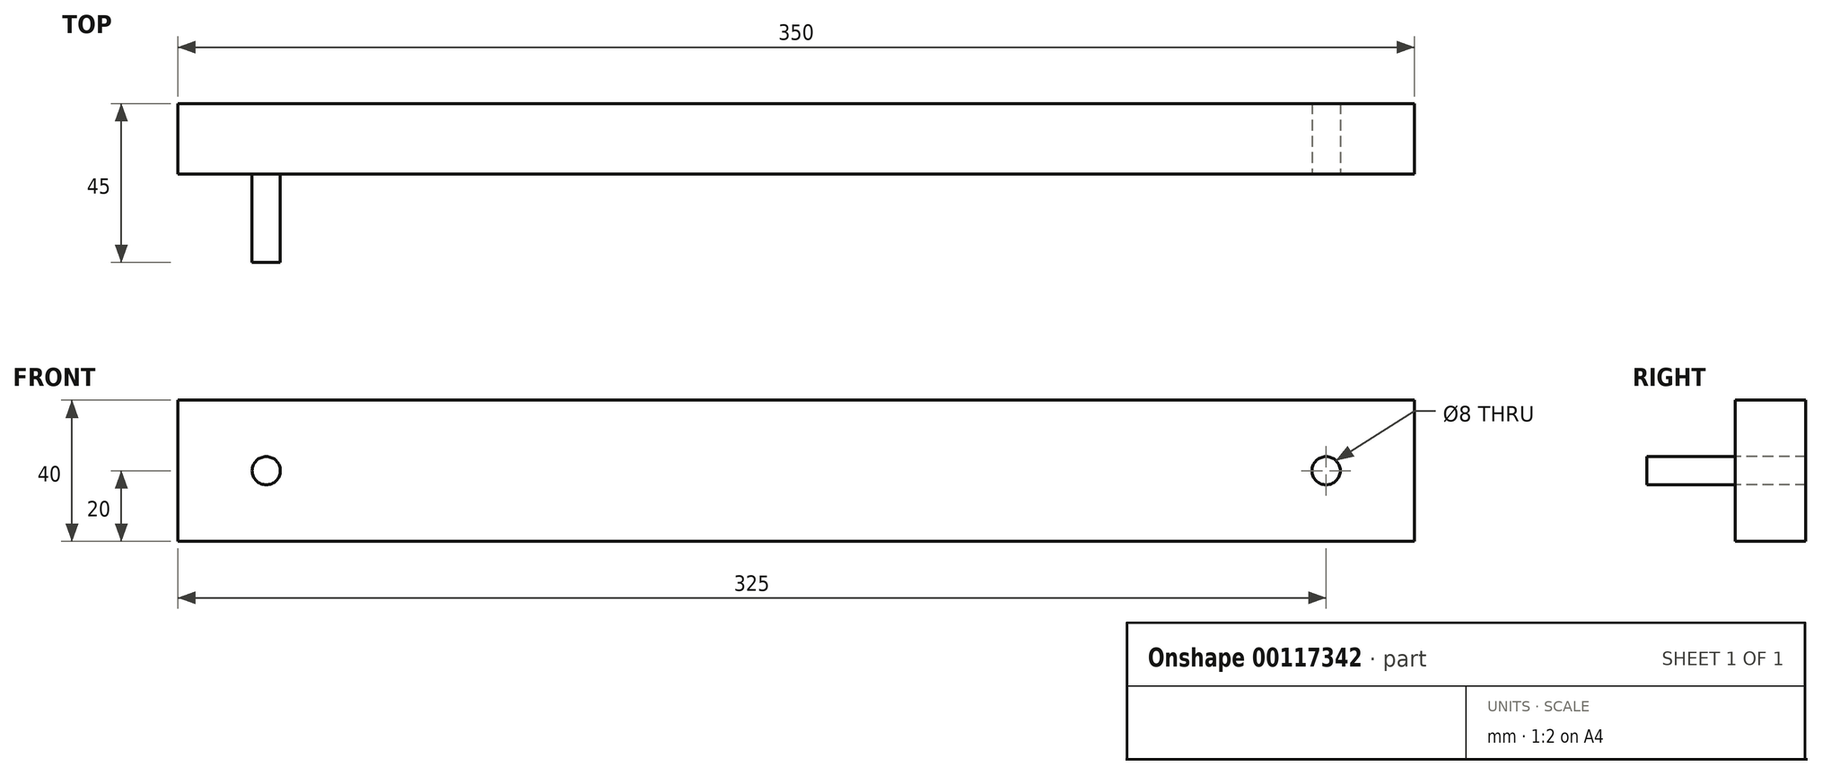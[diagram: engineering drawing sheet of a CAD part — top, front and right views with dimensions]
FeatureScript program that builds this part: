
annotation { "Feature Type Name" : "Feature", "Feature Type Description" : "" }
export const myFeature = defineFeature(function(context is Context, id is Id, definition is map)
    precondition{}
    {
        {
            var Q0;
            Q0=qCreatedBy(makeId("Front.planeOp"),FACE);
            var sketch = newSketch(context, id + "F0", { "sketchPlane" : qUnion([Q0])});
            skLineSegment(sketch, "E0.bottom", {"start": v(175, -20) * mm, "end": v(-175, -20) * mm});
            skLineSegment(sketch, "E0.top", {"start": v(175, 20) * mm, "end": v(-175, 20) * mm});
            skLineSegment(sketch, "E0.left", {"start": v(175, -20) * mm, "end": v(175, 20) * mm});
            skLineSegment(sketch, "E0.right", {"start": v(-175, -20) * mm, "end": v(-175, 20) * mm});
            skPoint(sketch, "E0.middle", {"position": v(0, 0) * mm});
            skSolve(sketch);
        }
        {
            var Q0;
            Q0 = qSketchRegion(id + "F0", true);
            extrude(context, id + "F1", {"entities" : qUnion([Q0]), "depth" : 20 * mm});
        }
        {
            var Q0;
            Q0=makeQuery(id+"F1.opExtrude","CAP_FACE",FACE,{"disambiguationData":[OSD([sQuery(id+"F0.wireOp",EDGE,"E0.bottom"),sQuery(id+"F0.wireOp",EDGE,"E0.top"),sQuery(id+"F0.wireOp",EDGE,"E0.left"),sQuery(id+"F0.wireOp",EDGE,"E0.right")])],"isStart":false});
            var sketch = newSketch(context, id + "F2", { "sketchPlane" : qUnion([Q0])});
            skCircle(sketch, "E1", {"center": v(-150, 0) * mm, "radius": 4 * mm});
            skPoint(sketch, "E1.centerSnap0", {"position": v(-175, 0) * mm});
            skPoint(sketch, "E2.centerSnap0", {"position": v(175, 0) * mm});
            skSolve(sketch);
        }
        {
            var Q0;
            Q0 = qSketchRegion(id + "F2", true);
            extrude(context, id + "F3", {"entities" : qUnion([Q0]), "operationType" : NewBodyOperationType.ADD, "depth" : 25 * mm});
        }
        {
            var Q0;
            Q0=makeQuery(id+"F1.opExtrude","CAP_FACE",FACE,{"disambiguationData":[OSD([sQuery(id+"F0.wireOp",EDGE,"E0.bottom"),sQuery(id+"F0.wireOp",EDGE,"E0.top"),sQuery(id+"F0.wireOp",EDGE,"E0.left"),sQuery(id+"F0.wireOp",EDGE,"E0.right")])],"isStart":false});
            var sketch = newSketch(context, id + "F4", { "sketchPlane" : qUnion([Q0])});
            skCircle(sketch, "E3", {"center": v(150, 0) * mm, "radius": 4 * mm});
            skPoint(sketch, "E3.centerSnap0", {"position": v(175, 0) * mm});
            skSolve(sketch);
        }
        {
            var Q0;
            Q0 = qSketchRegion(id + "F4", true);
            extrude(context, id + "F5", {"entities" : qUnion([Q0]), "operationType" : NewBodyOperationType.REMOVE, "oppositeDirection" : true, "depth" : 25 * mm});
        }
    });
